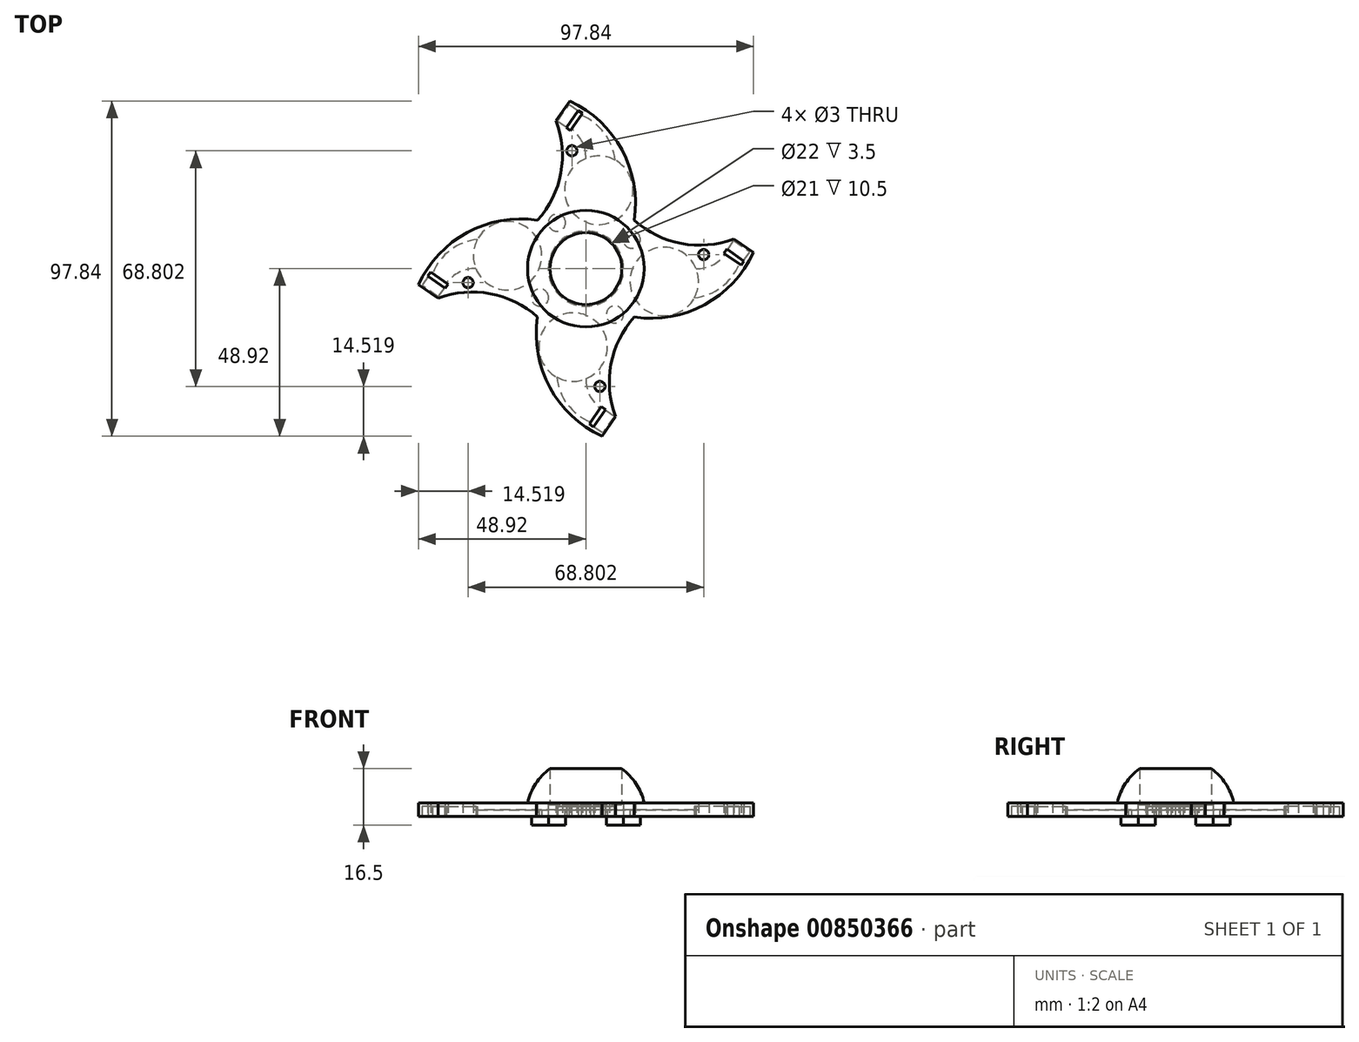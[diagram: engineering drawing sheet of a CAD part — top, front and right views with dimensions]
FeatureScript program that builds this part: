
annotation { "Feature Type Name" : "Feature", "Feature Type Description" : "" }
export const myFeature = defineFeature(function(context is Context, id is Id, definition is map)
    precondition{}
    {
        {
            var Q0;
            Q0=qCreatedBy(makeId("Top.planeOp"),FACE);
            var sketch = newSketch(context, id + "F0", { "sketchPlane" : qUnion([Q0])});
            skCircle(sketch, "E0", {"center": v(0, 0) * mm, "radius": 17.5 * mm});
            skLineSegment(sketch, "E1", {"start": v(0, 17.5) * mm, "end": v(0, -17.5) * mm});
            skSolve(sketch);
        }
        {
            var Q0;
            {var subQ0=sQuery(id+"F0.wireOp",EDGE,"E1");Q0=makeQuery(id+"F0.imprint","IMPRINT",FACE,{"disambiguationData":[TD([[makeQuery(id+"F0.imprint","IMPRINT",EDGE,{"derivedFrom":subQ0}),1.0]])]});}
            var Q1;
            Q1=sQuery(id+"F0.wireOp",EDGE,"E1");
            revolve(context, id + "F1", {"surfaceOperationType" : NewSurfaceOperationType.NEW, "entities" : qUnion([Q0]), "axis" : qUnion([Q1]), "revolveType" : RevolveType.ONE_DIRECTION, "angle" : 180 * degree});
        }
        {
            var Q0;
            Q0=makeQuery(id+"F1.opRevolve","CAP_FACE",FACE,{"disambiguationData":[OSD([sQuery(id+"F0.wireOp",EDGE,"E0"),sQuery(id+"F0.wireOp",EDGE,"E1")])],"isStart":true});
            var sketch = newSketch(context, id + "F2", { "sketchPlane" : qUnion([Q0])});
            skCircle(sketch, "E2", {"center": v(0, 0) * mm, "radius": 11 * mm});
            skSolve(sketch);
        }
        {
            var Q0;
            Q0 = qSketchRegion(id + "F2", true);
            extrude(context, id + "F3", {"entities" : qUnion([Q0]), "operationType" : NewBodyOperationType.REMOVE, "oppositeDirection" : true, "depth" : 3.5 * mm, "offsetDistance" : 25 * mm});
        }
        {
            var Q0;
            Q0=makeQuery(id+"F3.boolean.opBoolean","COPY",FACE,{"derivedFrom":makeQuery(id+"F3.opExtrude","CAP_FACE",FACE,{"disambiguationData":[OSD([sQuery(id+"F2.wireOp",EDGE,"E2")])],"isStart":false})});
            var sketch = newSketch(context, id + "F4", { "sketchPlane" : qUnion([Q0])});
            skCircle(sketch, "E3", {"center": v(0, 0) * mm, "radius": 10.5 * mm});
            skSolve(sketch);
        }
        {
            var Q0;
            Q0 = qSketchRegion(id + "F4", true);
            extrude(context, id + "F5", {"entities" : qUnion([Q0]), "operationType" : NewBodyOperationType.REMOVE, "oppositeDirection" : true, "depth" : 17 * mm, "offsetDistance" : 25 * mm});
        }
        {
            var Q0;
            Q0=makeQuery(id+"F1.opRevolve","CAP_FACE",FACE,{"disambiguationData":[OSD([sQuery(id+"F0.wireOp",EDGE,"E0"),sQuery(id+"F0.wireOp",EDGE,"E1")])],"isStart":true});
            var sketch = newSketch(context, id + "F6", { "sketchPlane" : qUnion([Q0])});
            skLineSegment(sketch, "E4", {"start": v(-12.37, 12.37) * mm, "end": v(-14.14, 14.14) * mm});
            skLineSegment(sketch, "E5.MirrorCS", {"start": v(12.37, 12.37) * mm, "end": v(14.14, 14.14) * mm});
            skPoint(sketch, "E6.orphan", {"position": v(0, 0) * mm});
            skArc(sketch, "E7", {"start": v(4.67, 48.92) * mm, "mid": v(-10.53, 34.66) * mm, "end": v(-14.14, 14.14) * mm});
            skArc(sketch, "E8", {"start": v(8.68, 43.18) * mm, "mid": v(7.32, 27.9) * mm, "end": v(14.14, 14.14) * mm});
            skLineSegment(sketch, "E9", {"start": v(4.67, 48.92) * mm, "end": v(8.68, 43.18) * mm});
            skArc(sketch, "E10", {"start": v(12.37, 12.37) * mm, "mid": v(0, 17.5) * mm, "end": v(-12.37, 12.37) * mm});
            skArc(sketch, "E11.1.0", {"start": v(-48.92, 4.67) * mm, "mid": v(-34.66, -10.53) * mm, "end": v(-14.14, -14.14) * mm});
            skArc(sketch, "E11.1.1", {"start": v(-43.18, 8.68) * mm, "mid": v(-27.9, 7.32) * mm, "end": v(-14.14, 14.14) * mm});
            skLineSegment(sketch, "E11.1.2", {"start": v(-48.92, 4.67) * mm, "end": v(-43.18, 8.68) * mm});
            skArc(sketch, "E11.1.3", {"start": v(-12.37, 12.37) * mm, "mid": v(-17.5, 0) * mm, "end": v(-12.37, -12.37) * mm});
            skLineSegment(sketch, "E11.1.5", {"start": v(-12.37, -12.37) * mm, "end": v(-14.14, -14.14) * mm});
            skArc(sketch, "E11.2.0", {"start": v(-4.67, -48.92) * mm, "mid": v(10.53, -34.66) * mm, "end": v(14.14, -14.14) * mm});
            skArc(sketch, "E11.2.1", {"start": v(-8.68, -43.18) * mm, "mid": v(-7.32, -27.9) * mm, "end": v(-14.14, -14.14) * mm});
            skLineSegment(sketch, "E11.2.2", {"start": v(-4.67, -48.92) * mm, "end": v(-8.68, -43.18) * mm});
            skArc(sketch, "E11.2.3", {"start": v(-12.37, -12.37) * mm, "mid": v(0, -17.5) * mm, "end": v(12.37, -12.37) * mm});
            skLineSegment(sketch, "E11.2.4", {"start": v(-12.37, -12.37) * mm, "end": v(-14.14, -14.14) * mm});
            skLineSegment(sketch, "E11.2.5", {"start": v(12.37, -12.37) * mm, "end": v(14.14, -14.14) * mm});
            skArc(sketch, "E11.3.0", {"start": v(48.92, -4.67) * mm, "mid": v(34.66, 10.53) * mm, "end": v(14.14, 14.14) * mm});
            skArc(sketch, "E11.3.1", {"start": v(43.18, -8.68) * mm, "mid": v(27.9, -7.32) * mm, "end": v(14.14, -14.14) * mm});
            skLineSegment(sketch, "E11.3.2", {"start": v(48.92, -4.67) * mm, "end": v(43.18, -8.68) * mm});
            skArc(sketch, "E11.3.3", {"start": v(12.37, -12.37) * mm, "mid": v(17.5, 0) * mm, "end": v(12.37, 12.37) * mm});
            skLineSegment(sketch, "E11.3.4", {"start": v(12.37, -12.37) * mm, "end": v(14.14, -14.14) * mm});
            skSolve(sketch);
        }
        {
            var Q0;
            Q0 = qSketchRegion(id + "F6", true);
            extrude(context, id + "F7", {"entities" : qUnion([Q0]), "oppositeDirection" : true, "depth" : 4 * mm, "offsetDistance" : 25 * mm});
        }
        {
            var Q0;
            Q0=makeQuery(id+"F7.opExtrude","CAP_FACE",FACE,{"disambiguationData":[OSD([sQuery(id+"F6.wireOp",EDGE,"E7"),sQuery(id+"F6.wireOp",EDGE,"E8"),sQuery(id+"F6.wireOp",EDGE,"E9"),sQuery(id+"F6.wireOp",EDGE,"E10"),sQuery(id+"F6.wireOp",EDGE,"E11.1.0"),sQuery(id+"F6.wireOp",EDGE,"E11.1.1"),sQuery(id+"F6.wireOp",EDGE,"E11.1.2"),sQuery(id+"F6.wireOp",EDGE,"E11.1.3"),sQuery(id+"F6.wireOp",EDGE,"E11.2.0"),sQuery(id+"F6.wireOp",EDGE,"E11.2.1"),sQuery(id+"F6.wireOp",EDGE,"E11.2.2"),sQuery(id+"F6.wireOp",EDGE,"E11.2.3"),sQuery(id+"F6.wireOp",EDGE,"E11.3.0"),sQuery(id+"F6.wireOp",EDGE,"E11.3.1"),sQuery(id+"F6.wireOp",EDGE,"E11.3.2"),sQuery(id+"F6.wireOp",EDGE,"E11.3.3")])],"isStart":true});
            var sketch = newSketch(context, id + "F8", { "sketchPlane" : qUnion([Q0])});
            skCircle(sketch, "E12", {"center": v(0, 0) * mm, "radius": 18.64 * mm});
            skCircle(sketch, "E13", {"center": v(0, 0) * mm, "radius": 11 * mm});
            skSolve(sketch);
        }
        {
            var Q0;
            Q0 = qSketchRegion(id + "F8", true);
            var Q1;
            Q1=makeQuery(id+"F7.opExtrude","CAP_FACE",FACE,{"disambiguationData":[OSD([sQuery(id+"F6.wireOp",EDGE,"E7"),sQuery(id+"F6.wireOp",EDGE,"E8"),sQuery(id+"F6.wireOp",EDGE,"E9"),sQuery(id+"F6.wireOp",EDGE,"E10"),sQuery(id+"F6.wireOp",EDGE,"E11.1.0"),sQuery(id+"F6.wireOp",EDGE,"E11.1.1"),sQuery(id+"F6.wireOp",EDGE,"E11.1.2"),sQuery(id+"F6.wireOp",EDGE,"E11.1.3"),sQuery(id+"F6.wireOp",EDGE,"E11.2.0"),sQuery(id+"F6.wireOp",EDGE,"E11.2.1"),sQuery(id+"F6.wireOp",EDGE,"E11.2.2"),sQuery(id+"F6.wireOp",EDGE,"E11.2.3"),sQuery(id+"F6.wireOp",EDGE,"E11.3.0"),sQuery(id+"F6.wireOp",EDGE,"E11.3.1"),sQuery(id+"F6.wireOp",EDGE,"E11.3.2"),sQuery(id+"F6.wireOp",EDGE,"E11.3.3")])],"isStart":false});
            extrude(context, id + "F9", {"entities" : qUnion([Q0]), "operationType" : NewBodyOperationType.ADD, "endBound" : BoundingType.UP_TO_SURFACE, "oppositeDirection" : true, "depth" : 25 * mm, "endBoundEntityFace" : qUnion([Q1]), "offsetDistance" : 25 * mm});
        }
        {
            var Q0;
            Q0=makeQuery(id+"F9.boolean.opBoolean","MERGE",FACE,{"derivedFrom":[makeQuery(id+"F1.opRevolve","CAP_FACE",FACE,{"disambiguationData":[OSD([sQuery(id+"F0.wireOp",EDGE,"E0"),sQuery(id+"F0.wireOp",EDGE,"E1")])],"isStart":true}),makeQuery(id+"F7.opExtrude","CAP_FACE",FACE,{"disambiguationData":[OSD([sQuery(id+"F6.wireOp",EDGE,"E7"),sQuery(id+"F6.wireOp",EDGE,"E8"),sQuery(id+"F6.wireOp",EDGE,"E9"),sQuery(id+"F6.wireOp",EDGE,"E10"),sQuery(id+"F6.wireOp",EDGE,"E11.1.0"),sQuery(id+"F6.wireOp",EDGE,"E11.1.1"),sQuery(id+"F6.wireOp",EDGE,"E11.1.2"),sQuery(id+"F6.wireOp",EDGE,"E11.1.3"),sQuery(id+"F6.wireOp",EDGE,"E11.2.0"),sQuery(id+"F6.wireOp",EDGE,"E11.2.1"),sQuery(id+"F6.wireOp",EDGE,"E11.2.2"),sQuery(id+"F6.wireOp",EDGE,"E11.2.3"),sQuery(id+"F6.wireOp",EDGE,"E11.3.0"),sQuery(id+"F6.wireOp",EDGE,"E11.3.1"),sQuery(id+"F6.wireOp",EDGE,"E11.3.2"),sQuery(id+"F6.wireOp",EDGE,"E11.3.3")])],"isStart":true}),makeQuery(id+"F9.opExtrude","CAP_FACE",FACE,{"disambiguationData":[OSD([sQuery(id+"F8.wireOp",EDGE,"E12"),sQuery(id+"F8.wireOp",EDGE,"E13")])],"isStart":true})]});
            var sketch = newSketch(context, id + "F10", { "sketchPlane" : qUnion([Q0])});
            skCircle(sketch, "E14", {"center": v(-3.75, 22.88) * mm, "radius": 10 * mm});
            skCircle(sketch, "E15.1.0", {"center": v(-22.88, -3.75) * mm, "radius": 10 * mm});
            skCircle(sketch, "E15.2.0", {"center": v(3.75, -22.88) * mm, "radius": 10 * mm});
            skCircle(sketch, "E15.3.0", {"center": v(22.88, 3.75) * mm, "radius": 10 * mm});
            skPoint(sketch, "E15.center", {"position": v(0, 0) * mm});
            skSolve(sketch);
        }
        {
            var Q0;
            Q0 = qSketchRegion(id + "F10", true);
            extrude(context, id + "F11", {"entities" : qUnion([Q0]), "operationType" : NewBodyOperationType.REMOVE, "oppositeDirection" : true, "depth" : 2 * mm, "offsetDistance" : 25 * mm});
        }
        {
            var Q0;
            Q0=makeQuery(id+"F9.boolean.opBoolean","MERGE",FACE,{"derivedFrom":[makeQuery(id+"F1.opRevolve","CAP_FACE",FACE,{"disambiguationData":[OSD([sQuery(id+"F0.wireOp",EDGE,"E0"),sQuery(id+"F0.wireOp",EDGE,"E1")])],"isStart":true}),makeQuery(id+"F7.opExtrude","CAP_FACE",FACE,{"disambiguationData":[OSD([sQuery(id+"F6.wireOp",EDGE,"E7"),sQuery(id+"F6.wireOp",EDGE,"E8"),sQuery(id+"F6.wireOp",EDGE,"E9"),sQuery(id+"F6.wireOp",EDGE,"E10"),sQuery(id+"F6.wireOp",EDGE,"E11.1.0"),sQuery(id+"F6.wireOp",EDGE,"E11.1.1"),sQuery(id+"F6.wireOp",EDGE,"E11.1.2"),sQuery(id+"F6.wireOp",EDGE,"E11.1.3"),sQuery(id+"F6.wireOp",EDGE,"E11.2.0"),sQuery(id+"F6.wireOp",EDGE,"E11.2.1"),sQuery(id+"F6.wireOp",EDGE,"E11.2.2"),sQuery(id+"F6.wireOp",EDGE,"E11.2.3"),sQuery(id+"F6.wireOp",EDGE,"E11.3.0"),sQuery(id+"F6.wireOp",EDGE,"E11.3.1"),sQuery(id+"F6.wireOp",EDGE,"E11.3.2"),sQuery(id+"F6.wireOp",EDGE,"E11.3.3")])],"isStart":true}),makeQuery(id+"F9.opExtrude","CAP_FACE",FACE,{"disambiguationData":[OSD([sQuery(id+"F8.wireOp",EDGE,"E12"),sQuery(id+"F8.wireOp",EDGE,"E13")])],"isStart":true})]});
            var sketch = newSketch(context, id + "F12", { "sketchPlane" : qUnion([Q0])});
            skLineSegment(sketch, "E16", {"start": v(8.24, 43.12) * mm, "end": v(5.94, 41.51) * mm});
            skLineSegment(sketch, "E17", {"start": v(2.62, 46.27) * mm, "end": v(4.92, 47.87) * mm});
            skLineSegment(sketch, "E18", {"start": v(5.94, 41.51) * mm, "end": v(5.62, 41.28) * mm});
            skLineSegment(sketch, "E19", {"start": v(5.62, 41.28) * mm, "end": v(2.3, 46.04) * mm});
            skLineSegment(sketch, "E20", {"start": v(2.3, 46.04) * mm, "end": v(2.62, 46.27) * mm});
            skLineSegment(sketch, "E21", {"start": v(8.24, 43.12) * mm, "end": v(4.92, 47.87) * mm});
            skLineSegment(sketch, "E22.1.0", {"start": v(-41.28, 5.62) * mm, "end": v(-46.04, 2.3) * mm});
            skLineSegment(sketch, "E22.1.1", {"start": v(-46.27, 2.62) * mm, "end": v(-47.87, 4.92) * mm});
            skLineSegment(sketch, "E22.1.2", {"start": v(-43.12, 8.24) * mm, "end": v(-47.87, 4.92) * mm});
            skLineSegment(sketch, "E22.1.3", {"start": v(-43.12, 8.24) * mm, "end": v(-41.51, 5.94) * mm});
            skLineSegment(sketch, "E22.1.4", {"start": v(-41.51, 5.94) * mm, "end": v(-41.28, 5.62) * mm});
            skLineSegment(sketch, "E22.1.5", {"start": v(-46.04, 2.3) * mm, "end": v(-46.27, 2.62) * mm});
            skLineSegment(sketch, "E22.2.0", {"start": v(-5.62, -41.28) * mm, "end": v(-2.3, -46.04) * mm});
            skLineSegment(sketch, "E22.2.1", {"start": v(-2.62, -46.27) * mm, "end": v(-4.92, -47.87) * mm});
            skLineSegment(sketch, "E22.2.2", {"start": v(-8.24, -43.12) * mm, "end": v(-4.92, -47.87) * mm});
            skLineSegment(sketch, "E22.2.3", {"start": v(-8.24, -43.12) * mm, "end": v(-5.94, -41.51) * mm});
            skLineSegment(sketch, "E22.2.4", {"start": v(-5.94, -41.51) * mm, "end": v(-5.62, -41.28) * mm});
            skLineSegment(sketch, "E22.2.5", {"start": v(-2.3, -46.04) * mm, "end": v(-2.62, -46.27) * mm});
            skLineSegment(sketch, "E22.3.0", {"start": v(41.28, -5.62) * mm, "end": v(46.04, -2.3) * mm});
            skLineSegment(sketch, "E22.3.1", {"start": v(46.27, -2.62) * mm, "end": v(47.87, -4.92) * mm});
            skLineSegment(sketch, "E22.3.2", {"start": v(43.12, -8.24) * mm, "end": v(47.87, -4.92) * mm});
            skLineSegment(sketch, "E22.3.3", {"start": v(43.12, -8.24) * mm, "end": v(41.51, -5.94) * mm});
            skLineSegment(sketch, "E22.3.4", {"start": v(41.51, -5.94) * mm, "end": v(41.28, -5.62) * mm});
            skLineSegment(sketch, "E22.3.5", {"start": v(46.04, -2.3) * mm, "end": v(46.27, -2.62) * mm});
            skPoint(sketch, "E22.center", {"position": v(0, 0) * mm});
            skSolve(sketch);
        }
        {
            var Q0;
            Q0 = qSketchRegion(id + "F12", true);
            extrude(context, id + "F13", {"entities" : qUnion([Q0]), "operationType" : NewBodyOperationType.REMOVE, "oppositeDirection" : true, "depth" : 3 * mm, "offsetDistance" : 25 * mm});
        }
        {
            var Q0;
            Q0=makeQuery(id+"F9.boolean.opBoolean","MERGE",FACE,{"derivedFrom":[makeQuery(id+"F1.opRevolve","CAP_FACE",FACE,{"disambiguationData":[OSD([sQuery(id+"F0.wireOp",EDGE,"E0"),sQuery(id+"F0.wireOp",EDGE,"E1")])],"isStart":true}),makeQuery(id+"F7.opExtrude","CAP_FACE",FACE,{"disambiguationData":[OSD([sQuery(id+"F6.wireOp",EDGE,"E7"),sQuery(id+"F6.wireOp",EDGE,"E8"),sQuery(id+"F6.wireOp",EDGE,"E9"),sQuery(id+"F6.wireOp",EDGE,"E10"),sQuery(id+"F6.wireOp",EDGE,"E11.1.0"),sQuery(id+"F6.wireOp",EDGE,"E11.1.1"),sQuery(id+"F6.wireOp",EDGE,"E11.1.2"),sQuery(id+"F6.wireOp",EDGE,"E11.1.3"),sQuery(id+"F6.wireOp",EDGE,"E11.2.0"),sQuery(id+"F6.wireOp",EDGE,"E11.2.1"),sQuery(id+"F6.wireOp",EDGE,"E11.2.2"),sQuery(id+"F6.wireOp",EDGE,"E11.2.3"),sQuery(id+"F6.wireOp",EDGE,"E11.3.0"),sQuery(id+"F6.wireOp",EDGE,"E11.3.1"),sQuery(id+"F6.wireOp",EDGE,"E11.3.2"),sQuery(id+"F6.wireOp",EDGE,"E11.3.3")])],"isStart":true}),makeQuery(id+"F9.opExtrude","CAP_FACE",FACE,{"disambiguationData":[OSD([sQuery(id+"F8.wireOp",EDGE,"E12"),sQuery(id+"F8.wireOp",EDGE,"E13")])],"isStart":true})]});
            var sketch = newSketch(context, id + "F14", { "sketchPlane" : qUnion([Q0])});
            skLineSegment(sketch, "E23", {"start": v(2.3, 46.04) * mm, "end": v(2.2, 46.16) * mm});
            skLineSegment(sketch, "E24", {"start": v(2.2, 46.16) * mm, "end": v(0.98, 45.3) * mm});
            skLineSegment(sketch, "E25", {"start": v(0.98, 45.3) * mm, "end": v(4.42, 40.38) * mm});
            skPoint(sketch, "E26.center", {"position": v(0, 0.02) * mm});
            skLineSegment(sketch, "E27", {"start": v(4.42, 40.38) * mm, "end": v(4.5, 40.26) * mm});
            skLineSegment(sketch, "E28", {"start": v(4.5, 40.26) * mm, "end": v(5.73, 41.12) * mm});
            skLineSegment(sketch, "E29", {"start": v(5.73, 41.12) * mm, "end": v(2.3, 46.04) * mm});
            skLineSegment(sketch, "E30.1.0", {"start": v(-45.3, 0.98) * mm, "end": v(-40.38, 4.42) * mm});
            skLineSegment(sketch, "E30.1.1", {"start": v(-40.26, 4.5) * mm, "end": v(-41.12, 5.73) * mm});
            skLineSegment(sketch, "E30.1.2", {"start": v(-41.12, 5.73) * mm, "end": v(-46.04, 2.3) * mm});
            skLineSegment(sketch, "E30.1.3", {"start": v(-46.16, 2.2) * mm, "end": v(-45.3, 0.98) * mm});
            skLineSegment(sketch, "E30.1.4", {"start": v(-40.38, 4.42) * mm, "end": v(-40.26, 4.5) * mm});
            skLineSegment(sketch, "E30.1.5", {"start": v(-46.04, 2.3) * mm, "end": v(-46.16, 2.2) * mm});
            skLineSegment(sketch, "E30.2.0", {"start": v(-0.98, -45.3) * mm, "end": v(-4.42, -40.38) * mm});
            skLineSegment(sketch, "E30.2.1", {"start": v(-4.5, -40.26) * mm, "end": v(-5.73, -41.12) * mm});
            skLineSegment(sketch, "E30.2.2", {"start": v(-5.73, -41.12) * mm, "end": v(-2.3, -46.04) * mm});
            skLineSegment(sketch, "E30.2.3", {"start": v(-2.2, -46.16) * mm, "end": v(-0.98, -45.3) * mm});
            skLineSegment(sketch, "E30.2.4", {"start": v(-4.42, -40.38) * mm, "end": v(-4.5, -40.26) * mm});
            skLineSegment(sketch, "E30.2.5", {"start": v(-2.3, -46.04) * mm, "end": v(-2.2, -46.16) * mm});
            skLineSegment(sketch, "E30.3.0", {"start": v(45.3, -0.98) * mm, "end": v(40.38, -4.42) * mm});
            skLineSegment(sketch, "E30.3.1", {"start": v(40.26, -4.5) * mm, "end": v(41.12, -5.73) * mm});
            skLineSegment(sketch, "E30.3.2", {"start": v(41.12, -5.73) * mm, "end": v(46.04, -2.3) * mm});
            skLineSegment(sketch, "E30.3.3", {"start": v(46.16, -2.2) * mm, "end": v(45.3, -0.98) * mm});
            skLineSegment(sketch, "E30.3.4", {"start": v(40.38, -4.42) * mm, "end": v(40.26, -4.5) * mm});
            skLineSegment(sketch, "E30.3.5", {"start": v(46.04, -2.3) * mm, "end": v(46.16, -2.2) * mm});
            skPoint(sketch, "E30.center", {"position": v(0, 0) * mm});
            skSolve(sketch);
        }
        {
            var Q0;
            Q0 = qSketchRegion(id + "F14", true);
            extrude(context, id + "F15", {"entities" : qUnion([Q0]), "operationType" : NewBodyOperationType.REMOVE, "oppositeDirection" : true, "depth" : 25 * mm, "offsetDistance" : 25 * mm});
        }
        {
            var Q0;
            Q0=makeQuery(id+"F9.boolean.opBoolean","MERGE",FACE,{"derivedFrom":[makeQuery(id+"F1.opRevolve","CAP_FACE",FACE,{"disambiguationData":[OSD([sQuery(id+"F0.wireOp",EDGE,"E0"),sQuery(id+"F0.wireOp",EDGE,"E1")])],"isStart":true}),makeQuery(id+"F7.opExtrude","CAP_FACE",FACE,{"disambiguationData":[OSD([sQuery(id+"F6.wireOp",EDGE,"E7"),sQuery(id+"F6.wireOp",EDGE,"E8"),sQuery(id+"F6.wireOp",EDGE,"E9"),sQuery(id+"F6.wireOp",EDGE,"E10"),sQuery(id+"F6.wireOp",EDGE,"E11.1.0"),sQuery(id+"F6.wireOp",EDGE,"E11.1.1"),sQuery(id+"F6.wireOp",EDGE,"E11.1.2"),sQuery(id+"F6.wireOp",EDGE,"E11.1.3"),sQuery(id+"F6.wireOp",EDGE,"E11.2.0"),sQuery(id+"F6.wireOp",EDGE,"E11.2.1"),sQuery(id+"F6.wireOp",EDGE,"E11.2.2"),sQuery(id+"F6.wireOp",EDGE,"E11.2.3"),sQuery(id+"F6.wireOp",EDGE,"E11.3.0"),sQuery(id+"F6.wireOp",EDGE,"E11.3.1"),sQuery(id+"F6.wireOp",EDGE,"E11.3.2"),sQuery(id+"F6.wireOp",EDGE,"E11.3.3")])],"isStart":true}),makeQuery(id+"F9.opExtrude","CAP_FACE",FACE,{"disambiguationData":[OSD([sQuery(id+"F8.wireOp",EDGE,"E12"),sQuery(id+"F8.wireOp",EDGE,"E13")])],"isStart":true})]});
            var sketch = newSketch(context, id + "F16", { "sketchPlane" : qUnion([Q0])});
            skArc(sketch, "E31", {"start": v(1.34, 44.78) * mm, "mid": v(-5.4, 39.58) * mm, "end": v(-8.54, 31.67) * mm});
            skArc(sketch, "E32", {"start": v(4.18, 40.72) * mm, "mid": v(1.05, 36.94) * mm, "end": v(0, 32.15) * mm});
            skLineSegment(sketch, "E33", {"start": v(4.18, 40.72) * mm, "end": v(1.34, 44.78) * mm});
            skArc(sketch, "E34", {"start": v(0, 32.15) * mm, "mid": v(-4.32, 32.87) * mm, "end": v(-8.54, 31.67) * mm});
            skArc(sketch, "E35.1.0", {"start": v(-44.78, 1.34) * mm, "mid": v(-39.58, -5.4) * mm, "end": v(-31.67, -8.54) * mm});
            skArc(sketch, "E35.1.1", {"start": v(-40.72, 4.18) * mm, "mid": v(-36.94, 1.05) * mm, "end": v(-32.15, 0) * mm});
            skArc(sketch, "E35.1.2", {"start": v(-32.15, 0) * mm, "mid": v(-32.87, -4.32) * mm, "end": v(-31.67, -8.54) * mm});
            skLineSegment(sketch, "E35.1.3", {"start": v(-40.72, 4.18) * mm, "end": v(-44.78, 1.34) * mm});
            skArc(sketch, "E35.2.0", {"start": v(-1.34, -44.78) * mm, "mid": v(5.4, -39.58) * mm, "end": v(8.54, -31.67) * mm});
            skArc(sketch, "E35.2.1", {"start": v(-4.18, -40.72) * mm, "mid": v(-1.05, -36.94) * mm, "end": v(0, -32.15) * mm});
            skArc(sketch, "E35.2.2", {"start": v(0, -32.15) * mm, "mid": v(4.32, -32.87) * mm, "end": v(8.54, -31.67) * mm});
            skLineSegment(sketch, "E35.2.3", {"start": v(-4.18, -40.72) * mm, "end": v(-1.34, -44.78) * mm});
            skArc(sketch, "E35.3.0", {"start": v(44.78, -1.34) * mm, "mid": v(39.58, 5.4) * mm, "end": v(31.67, 8.54) * mm});
            skArc(sketch, "E35.3.1", {"start": v(40.72, -4.18) * mm, "mid": v(36.94, -1.05) * mm, "end": v(32.15, 0) * mm});
            skArc(sketch, "E35.3.2", {"start": v(32.15, 0) * mm, "mid": v(32.87, 4.32) * mm, "end": v(31.67, 8.54) * mm});
            skLineSegment(sketch, "E35.3.3", {"start": v(40.72, -4.18) * mm, "end": v(44.78, -1.34) * mm});
            skPoint(sketch, "E35.center", {"position": v(0, 0) * mm});
            skSolve(sketch);
        }
        {
            var Q0;
            Q0 = qSketchRegion(id + "F16", true);
            extrude(context, id + "F17", {"entities" : qUnion([Q0]), "operationType" : NewBodyOperationType.REMOVE, "oppositeDirection" : true, "depth" : 3 * mm, "offsetDistance" : 25 * mm});
        }
        {
            var Q0;
            Q0=makeQuery(id+"F9.boolean.opBoolean","MERGE",FACE,{"derivedFrom":[makeQuery(id+"F1.opRevolve","CAP_FACE",FACE,{"disambiguationData":[OSD([sQuery(id+"F0.wireOp",EDGE,"E0"),sQuery(id+"F0.wireOp",EDGE,"E1")])],"isStart":true}),makeQuery(id+"F7.opExtrude","CAP_FACE",FACE,{"disambiguationData":[OSD([sQuery(id+"F6.wireOp",EDGE,"E7"),sQuery(id+"F6.wireOp",EDGE,"E8"),sQuery(id+"F6.wireOp",EDGE,"E9"),sQuery(id+"F6.wireOp",EDGE,"E10"),sQuery(id+"F6.wireOp",EDGE,"E11.1.0"),sQuery(id+"F6.wireOp",EDGE,"E11.1.1"),sQuery(id+"F6.wireOp",EDGE,"E11.1.2"),sQuery(id+"F6.wireOp",EDGE,"E11.1.3"),sQuery(id+"F6.wireOp",EDGE,"E11.2.0"),sQuery(id+"F6.wireOp",EDGE,"E11.2.1"),sQuery(id+"F6.wireOp",EDGE,"E11.2.2"),sQuery(id+"F6.wireOp",EDGE,"E11.2.3"),sQuery(id+"F6.wireOp",EDGE,"E11.3.0"),sQuery(id+"F6.wireOp",EDGE,"E11.3.1"),sQuery(id+"F6.wireOp",EDGE,"E11.3.2"),sQuery(id+"F6.wireOp",EDGE,"E11.3.3")])],"isStart":true}),makeQuery(id+"F9.opExtrude","CAP_FACE",FACE,{"disambiguationData":[OSD([sQuery(id+"F8.wireOp",EDGE,"E12"),sQuery(id+"F8.wireOp",EDGE,"E13")])],"isStart":true})]});
            var sketch = newSketch(context, id + "F18", { "sketchPlane" : qUnion([Q0])});
            skCircle(sketch, "E36", {"center": v(8.45, 13.4) * mm, "radius": 2.5 * mm});
            skCircle(sketch, "E37.1.0", {"center": v(-13.4, 8.45) * mm, "radius": 2.5 * mm});
            skCircle(sketch, "E37.2.0", {"center": v(-8.45, -13.4) * mm, "radius": 2.5 * mm});
            skCircle(sketch, "E37.3.0", {"center": v(13.4, -8.45) * mm, "radius": 2.5 * mm});
            skPoint(sketch, "E37.center", {"position": v(0, 0) * mm});
            skSolve(sketch);
        }
        {
            var Q0;
            Q0 = qSketchRegion(id + "F18", true);
            extrude(context, id + "F19", {"entities" : qUnion([Q0]), "operationType" : NewBodyOperationType.ADD, "depth" : 2.5 * mm, "offsetDistance" : 25 * mm});
        }
        {
            var Q0;
            Q0=makeQuery(id+"F9.boolean.opBoolean","MERGE",FACE,{"derivedFrom":[makeQuery(id+"F1.opRevolve","CAP_FACE",FACE,{"disambiguationData":[OSD([sQuery(id+"F0.wireOp",EDGE,"E0"),sQuery(id+"F0.wireOp",EDGE,"E1")])],"isStart":true}),makeQuery(id+"F7.opExtrude","CAP_FACE",FACE,{"disambiguationData":[OSD([sQuery(id+"F6.wireOp",EDGE,"E7"),sQuery(id+"F6.wireOp",EDGE,"E8"),sQuery(id+"F6.wireOp",EDGE,"E9"),sQuery(id+"F6.wireOp",EDGE,"E10"),sQuery(id+"F6.wireOp",EDGE,"E11.1.0"),sQuery(id+"F6.wireOp",EDGE,"E11.1.1"),sQuery(id+"F6.wireOp",EDGE,"E11.1.2"),sQuery(id+"F6.wireOp",EDGE,"E11.1.3"),sQuery(id+"F6.wireOp",EDGE,"E11.2.0"),sQuery(id+"F6.wireOp",EDGE,"E11.2.1"),sQuery(id+"F6.wireOp",EDGE,"E11.2.2"),sQuery(id+"F6.wireOp",EDGE,"E11.2.3"),sQuery(id+"F6.wireOp",EDGE,"E11.3.0"),sQuery(id+"F6.wireOp",EDGE,"E11.3.1"),sQuery(id+"F6.wireOp",EDGE,"E11.3.2"),sQuery(id+"F6.wireOp",EDGE,"E11.3.3")])],"isStart":true}),makeQuery(id+"F9.opExtrude","CAP_FACE",FACE,{"disambiguationData":[OSD([sQuery(id+"F8.wireOp",EDGE,"E12"),sQuery(id+"F8.wireOp",EDGE,"E13")])],"isStart":true})]});
            var sketch = newSketch(context, id + "F20", { "sketchPlane" : qUnion([Q0])});
            skCircle(sketch, "E38", {"center": v(4.08, 34.4) * mm, "radius": 1.5 * mm});
            skCircle(sketch, "E39.1.0", {"center": v(-34.4, 4.08) * mm, "radius": 1.5 * mm});
            skCircle(sketch, "E39.2.0", {"center": v(-4.08, -34.4) * mm, "radius": 1.5 * mm});
            skCircle(sketch, "E39.3.0", {"center": v(34.4, -4.08) * mm, "radius": 1.5 * mm});
            skPoint(sketch, "E39.center", {"position": v(0, 0) * mm});
            skSolve(sketch);
        }
        {
            var Q0;
            Q0 = qSketchRegion(id + "F20", true);
            extrude(context, id + "F21", {"entities" : qUnion([Q0]), "operationType" : NewBodyOperationType.REMOVE, "oppositeDirection" : true, "depth" : 25 * mm, "offsetDistance" : 25 * mm});
        }
    });
